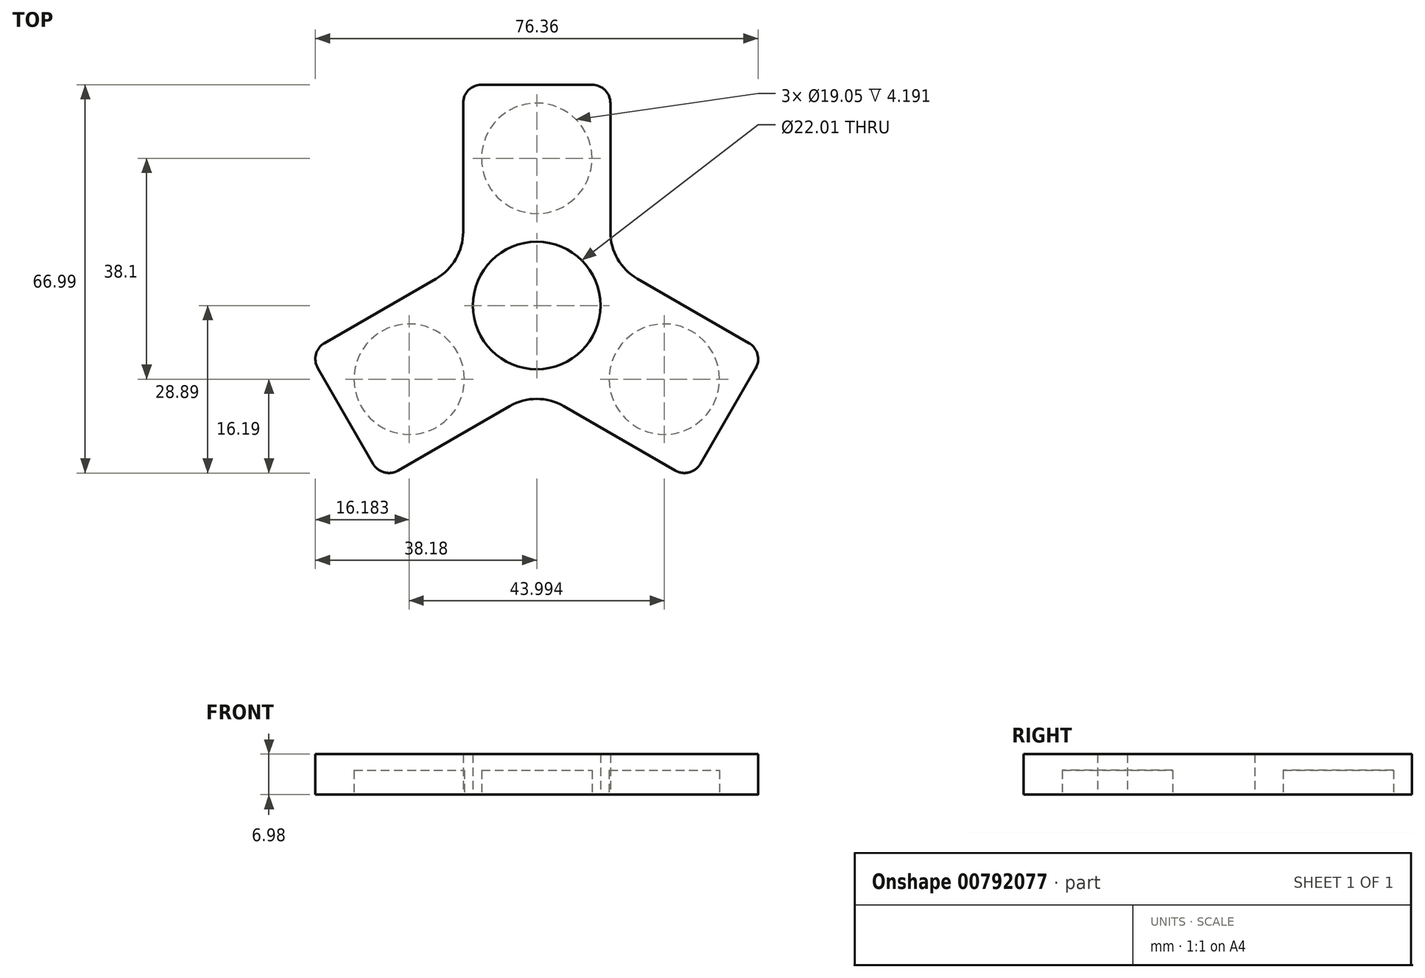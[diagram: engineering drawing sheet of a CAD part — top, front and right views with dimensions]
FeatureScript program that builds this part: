
annotation { "Feature Type Name" : "Feature", "Feature Type Description" : "" }
export const myFeature = defineFeature(function(context is Context, id is Id, definition is map)
    precondition{}
    {
        {
            var Q0;
            Q0=qCreatedBy(makeId("Top.planeOp"),FACE);
            var sketch = newSketch(context, id + "F0", { "sketchPlane" : qUnion([Q0])});
            skCircle(sketch, "E0", {"center": v(0, 0) * mm, "radius": 11 * mm});
            skLineSegment(sketch, "E1.bottom", {"start": v(-9.53, 38.1) * mm, "end": v(9.53, 38.1) * mm});
            skLineSegment(sketch, "E1.top", {"start": v(-12.7, 12.7) * mm, "end": v(12.7, 12.7) * mm});
            skLineSegment(sketch, "E1.left", {"start": v(-12.7, 34.92) * mm, "end": v(-12.7, 12.7) * mm});
            skLineSegment(sketch, "E1.right", {"start": v(12.7, 34.92) * mm, "end": v(12.7, 12.7) * mm});
            skLineSegment(sketch, "E2", {"start": v(0, 0) * mm, "end": v(0, 12.7) * mm});
            skLineSegment(sketch, "E3.1.0", {"start": v(-4.65, -17.35) * mm, "end": v(-17.35, 4.65) * mm});
            skLineSegment(sketch, "E3.1.1", {"start": v(-36.6, -6.46) * mm, "end": v(-17.35, 4.65) * mm});
            skLineSegment(sketch, "E3.1.2", {"start": v(-28.23, -27.3) * mm, "end": v(-37.76, -10.8) * mm});
            skLineSegment(sketch, "E3.1.3", {"start": v(-23.9, -28.46) * mm, "end": v(-4.65, -17.35) * mm});
            skLineSegment(sketch, "E3.2.0", {"start": v(17.35, 4.65) * mm, "end": v(4.65, -17.35) * mm});
            skLineSegment(sketch, "E3.2.1", {"start": v(23.9, -28.46) * mm, "end": v(4.65, -17.35) * mm});
            skLineSegment(sketch, "E3.2.2", {"start": v(37.76, -10.8) * mm, "end": v(28.23, -27.3) * mm});
            skLineSegment(sketch, "E3.2.3", {"start": v(36.6, -6.46) * mm, "end": v(17.35, 4.65) * mm});
            skArc(sketch, "E4", {"start": v(12.7, 12.7) * mm, "mid": v(13.95, 8.05) * mm, "end": v(17.35, 4.65) * mm});
            skArc(sketch, "E5", {"start": v(4.65, -17.35) * mm, "mid": v(0, -16.1) * mm, "end": v(-4.65, -17.35) * mm});
            skArc(sketch, "E6", {"start": v(-17.35, 4.65) * mm, "mid": v(-13.95, 8.05) * mm, "end": v(-12.7, 12.7) * mm});
            skPoint(sketch, "E7.visualSharp", {"position": v(-39.35, -8.05) * mm});
            skArc(sketch, "E7.filletArc", {"start": v(-36.6, -6.46) * mm, "mid": v(-38.08, -8.4) * mm, "end": v(-37.76, -10.8) * mm});
            skPoint(sketch, "E8.visualSharp", {"position": v(-26.65, -30.05) * mm});
            skArc(sketch, "E8.filletArc", {"start": v(-28.23, -27.3) * mm, "mid": v(-26.3, -28.78) * mm, "end": v(-23.9, -28.46) * mm});
            skPoint(sketch, "E9.visualSharp", {"position": v(26.65, -30.05) * mm});
            skArc(sketch, "E9.filletArc", {"start": v(23.9, -28.46) * mm, "mid": v(26.3, -28.78) * mm, "end": v(28.23, -27.3) * mm});
            skPoint(sketch, "E10.visualSharp", {"position": v(39.35, -8.05) * mm});
            skArc(sketch, "E10.filletArc", {"start": v(37.76, -10.8) * mm, "mid": v(38.08, -8.4) * mm, "end": v(36.6, -6.46) * mm});
            skPoint(sketch, "E11.visualSharp", {"position": v(12.7, 38.1) * mm});
            skArc(sketch, "E11.filletArc", {"start": v(12.7, 34.92) * mm, "mid": v(11.77, 37.17) * mm, "end": v(9.53, 38.1) * mm});
            skPoint(sketch, "E12.visualSharp", {"position": v(-12.7, 38.1) * mm});
            skArc(sketch, "E12.filletArc", {"start": v(-9.53, 38.1) * mm, "mid": v(-11.77, 37.17) * mm, "end": v(-12.7, 34.92) * mm});
            skSolve(sketch);
        }
        {
            var Q0;
            Q0 = qSketchRegion(id + "F0", true);
            extrude(context, id + "F1", {"entities" : qUnion([Q0]), "endBound" : BoundingType.SYMMETRIC, "depth" : 7 * mm, "offsetDistance" : 25.4 * mm});
        }
        {
            var Q0;
            Q0=makeQuery(id+"F1.opExtrude","CAP_FACE",FACE,{"disambiguationData":[OSD([sQuery(id+"F0.wireOp",EDGE,"E0"),sQuery(id+"F0.wireOp",EDGE,"E1.bottom"),sQuery(id+"F0.wireOp",EDGE,"E1.left"),sQuery(id+"F0.wireOp",EDGE,"E1.right"),sQuery(id+"F0.wireOp",EDGE,"E3.1.1"),sQuery(id+"F0.wireOp",EDGE,"E3.1.2"),sQuery(id+"F0.wireOp",EDGE,"E3.1.3"),sQuery(id+"F0.wireOp",EDGE,"E3.2.1"),sQuery(id+"F0.wireOp",EDGE,"E3.2.2"),sQuery(id+"F0.wireOp",EDGE,"E3.2.3"),sQuery(id+"F0.wireOp",EDGE,"E4"),sQuery(id+"F0.wireOp",EDGE,"E5"),sQuery(id+"F0.wireOp",EDGE,"E6"),sQuery(id+"F0.wireOp",EDGE,"E7.filletArc"),sQuery(id+"F0.wireOp",EDGE,"E8.filletArc"),sQuery(id+"F0.wireOp",EDGE,"E9.filletArc"),sQuery(id+"F0.wireOp",EDGE,"E10.filletArc"),sQuery(id+"F0.wireOp",EDGE,"E11.filletArc"),sQuery(id+"F0.wireOp",EDGE,"E12.filletArc")])],"isStart":false});
            var sketch = newSketch(context, id + "F2", { "sketchPlane" : qUnion([Q0])});
            skLineSegment(sketch, "E13.0.1.0", {"start": v(-12.7, 34.93) * mm, "end": v(12.7, 34.92) * mm});
            skLineSegment(sketch, "E13.0.2.0", {"start": v(-12.7, 31.75) * mm, "end": v(12.7, 31.75) * mm});
            skLineSegment(sketch, "E13.0.3.0", {"start": v(-12.7, 28.58) * mm, "end": v(12.7, 28.57) * mm});
            skLineSegment(sketch, "E13.0.4.0", {"start": v(-12.7, 25.4) * mm, "end": v(12.7, 25.4) * mm});
            skLineSegment(sketch, "E13.0.5.0", {"start": v(-12.7, 22.23) * mm, "end": v(12.7, 22.22) * mm});
            skLineSegment(sketch, "E13.0.6.0", {"start": v(-12.7, 19.05) * mm, "end": v(12.7, 19.05) * mm});
            skLineSegment(sketch, "E13.0.7.0", {"start": v(-12.7, 15.88) * mm, "end": v(12.7, 15.88) * mm});
            skLineSegment(sketch, "E13.0.8.0", {"start": v(-12.7, 12.7) * mm, "end": v(12.7, 12.7) * mm});
            skLineSegment(sketch, "E14.1.0.0", {"start": v(-9.52, 12.7) * mm, "end": v(-9.52, 38.1) * mm});
            skLineSegment(sketch, "E14.2.0.0", {"start": v(-6.35, 12.7) * mm, "end": v(-6.35, 38.1) * mm});
            skLineSegment(sketch, "E14.3.0.0", {"start": v(-3.17, 12.7) * mm, "end": v(-3.17, 38.1) * mm});
            skLineSegment(sketch, "E14.4.0.0", {"start": v(0, 12.7) * mm, "end": v(0, 38.1) * mm});
            skLineSegment(sketch, "E14.5.0.0", {"start": v(3.18, 12.7) * mm, "end": v(3.18, 38.1) * mm});
            skLineSegment(sketch, "E14.6.0.0", {"start": v(6.35, 12.7) * mm, "end": v(6.35, 38.1) * mm});
            skLineSegment(sketch, "E14.7.0.0", {"start": v(9.53, 12.7) * mm, "end": v(9.53, 38.1) * mm});
            skLineSegment(sketch, "E15.1.0", {"start": v(-14.17, -0.85) * mm, "end": v(-36.17, -13.55) * mm});
            skLineSegment(sketch, "E15.1.1", {"start": v(-15.76, 1.9) * mm, "end": v(-37.76, -10.8) * mm});
            skLineSegment(sketch, "E15.1.2", {"start": v(-12.59, -3.6) * mm, "end": v(-34.58, -16.3) * mm});
            skLineSegment(sketch, "E15.1.3", {"start": v(-11, -6.35) * mm, "end": v(-33, -19.05) * mm});
            skLineSegment(sketch, "E15.1.4", {"start": v(-9.41, -9.1) * mm, "end": v(-31.4, -21.8) * mm});
            skLineSegment(sketch, "E15.1.5", {"start": v(-7.82, -11.85) * mm, "end": v(-29.82, -24.55) * mm});
            skLineSegment(sketch, "E15.1.6", {"start": v(-6.24, -14.6) * mm, "end": v(-28.23, -27.3) * mm});
            skLineSegment(sketch, "E15.1.7", {"start": v(-7.4, -18.94) * mm, "end": v(-20.1, 3.06) * mm});
            skLineSegment(sketch, "E15.1.8", {"start": v(-10.15, -20.52) * mm, "end": v(-22.85, 1.47) * mm});
            skLineSegment(sketch, "E15.1.9", {"start": v(-12.9, -22.11) * mm, "end": v(-25.6, -0.11) * mm});
            skLineSegment(sketch, "E15.1.10", {"start": v(-15.65, -23.7) * mm, "end": v(-28.35, -1.7) * mm});
            skLineSegment(sketch, "E15.1.11", {"start": v(-18.4, -25.29) * mm, "end": v(-31.1, -3.29) * mm});
            skLineSegment(sketch, "E15.1.12", {"start": v(-21.15, -26.87) * mm, "end": v(-33.85, -4.88) * mm});
            skLineSegment(sketch, "E15.1.13", {"start": v(-23.9, -28.46) * mm, "end": v(-36.6, -6.46) * mm});
            skLineSegment(sketch, "E15.1.14", {"start": v(-4.65, -17.35) * mm, "end": v(-17.35, 4.65) * mm});
            skLineSegment(sketch, "E15.2.0", {"start": v(7.82, -11.85) * mm, "end": v(29.82, -24.55) * mm});
            skLineSegment(sketch, "E15.2.1", {"start": v(6.24, -14.6) * mm, "end": v(28.23, -27.3) * mm});
            skLineSegment(sketch, "E15.2.2", {"start": v(9.41, -9.1) * mm, "end": v(31.4, -21.8) * mm});
            skLineSegment(sketch, "E15.2.3", {"start": v(11, -6.35) * mm, "end": v(33, -19.05) * mm});
            skLineSegment(sketch, "E15.2.4", {"start": v(12.59, -3.6) * mm, "end": v(34.58, -16.3) * mm});
            skLineSegment(sketch, "E15.2.5", {"start": v(14.17, -0.85) * mm, "end": v(36.17, -13.55) * mm});
            skLineSegment(sketch, "E15.2.6", {"start": v(15.76, 1.9) * mm, "end": v(37.76, -10.8) * mm});
            skLineSegment(sketch, "E15.2.7", {"start": v(20.1, 3.06) * mm, "end": v(7.4, -18.94) * mm});
            skLineSegment(sketch, "E15.2.8", {"start": v(22.85, 1.47) * mm, "end": v(10.15, -20.52) * mm});
            skLineSegment(sketch, "E15.2.9", {"start": v(25.6, -0.11) * mm, "end": v(12.9, -22.11) * mm});
            skLineSegment(sketch, "E15.2.10", {"start": v(28.35, -1.7) * mm, "end": v(15.65, -23.7) * mm});
            skLineSegment(sketch, "E15.2.11", {"start": v(31.1, -3.29) * mm, "end": v(18.4, -25.29) * mm});
            skLineSegment(sketch, "E15.2.12", {"start": v(33.85, -4.88) * mm, "end": v(21.15, -26.87) * mm});
            skLineSegment(sketch, "E15.2.13", {"start": v(36.6, -6.46) * mm, "end": v(23.9, -28.46) * mm});
            skLineSegment(sketch, "E15.2.14", {"start": v(17.35, 4.65) * mm, "end": v(4.65, -17.35) * mm});
            skPoint(sketch, "E15.center", {"position": v(0, 0) * mm});
            skSolve(sketch);
        }
        {
            var Q0;
            Q0=makeQuery(id+"F1.opExtrude","CAP_FACE",FACE,{"disambiguationData":[OSD([sQuery(id+"F0.wireOp",EDGE,"E0"),sQuery(id+"F0.wireOp",EDGE,"E1.bottom"),sQuery(id+"F0.wireOp",EDGE,"E1.left"),sQuery(id+"F0.wireOp",EDGE,"E1.right"),sQuery(id+"F0.wireOp",EDGE,"E3.1.1"),sQuery(id+"F0.wireOp",EDGE,"E3.1.2"),sQuery(id+"F0.wireOp",EDGE,"E3.1.3"),sQuery(id+"F0.wireOp",EDGE,"E3.2.1"),sQuery(id+"F0.wireOp",EDGE,"E3.2.2"),sQuery(id+"F0.wireOp",EDGE,"E3.2.3"),sQuery(id+"F0.wireOp",EDGE,"E4"),sQuery(id+"F0.wireOp",EDGE,"E5"),sQuery(id+"F0.wireOp",EDGE,"E6"),sQuery(id+"F0.wireOp",EDGE,"E7.filletArc"),sQuery(id+"F0.wireOp",EDGE,"E8.filletArc"),sQuery(id+"F0.wireOp",EDGE,"E9.filletArc"),sQuery(id+"F0.wireOp",EDGE,"E10.filletArc"),sQuery(id+"F0.wireOp",EDGE,"E11.filletArc"),sQuery(id+"F0.wireOp",EDGE,"E12.filletArc")])],"isStart":true});
            var sketch = newSketch(context, id + "F3", { "sketchPlane" : qUnion([Q0])});
            skCircle(sketch, "E16", {"center": v(0, -25.4) * mm, "radius": 9.53 * mm});
            skCircle(sketch, "E17.1.0", {"center": v(22, 12.7) * mm, "radius": 9.53 * mm});
            skCircle(sketch, "E17.2.0", {"center": v(-22, 12.7) * mm, "radius": 9.53 * mm});
            skPoint(sketch, "E17.center", {"position": v(0, 0) * mm});
            skSolve(sketch);
        }
        {
            var Q0;
            Q0 = qSketchRegion(id + "F3", true);
            extrude(context, id + "F4", {"entities" : qUnion([Q0]), "operationType" : NewBodyOperationType.REMOVE, "oppositeDirection" : true, "depth" : 4.2 * mm, "offsetDistance" : 25.4 * mm});
        }
    });
